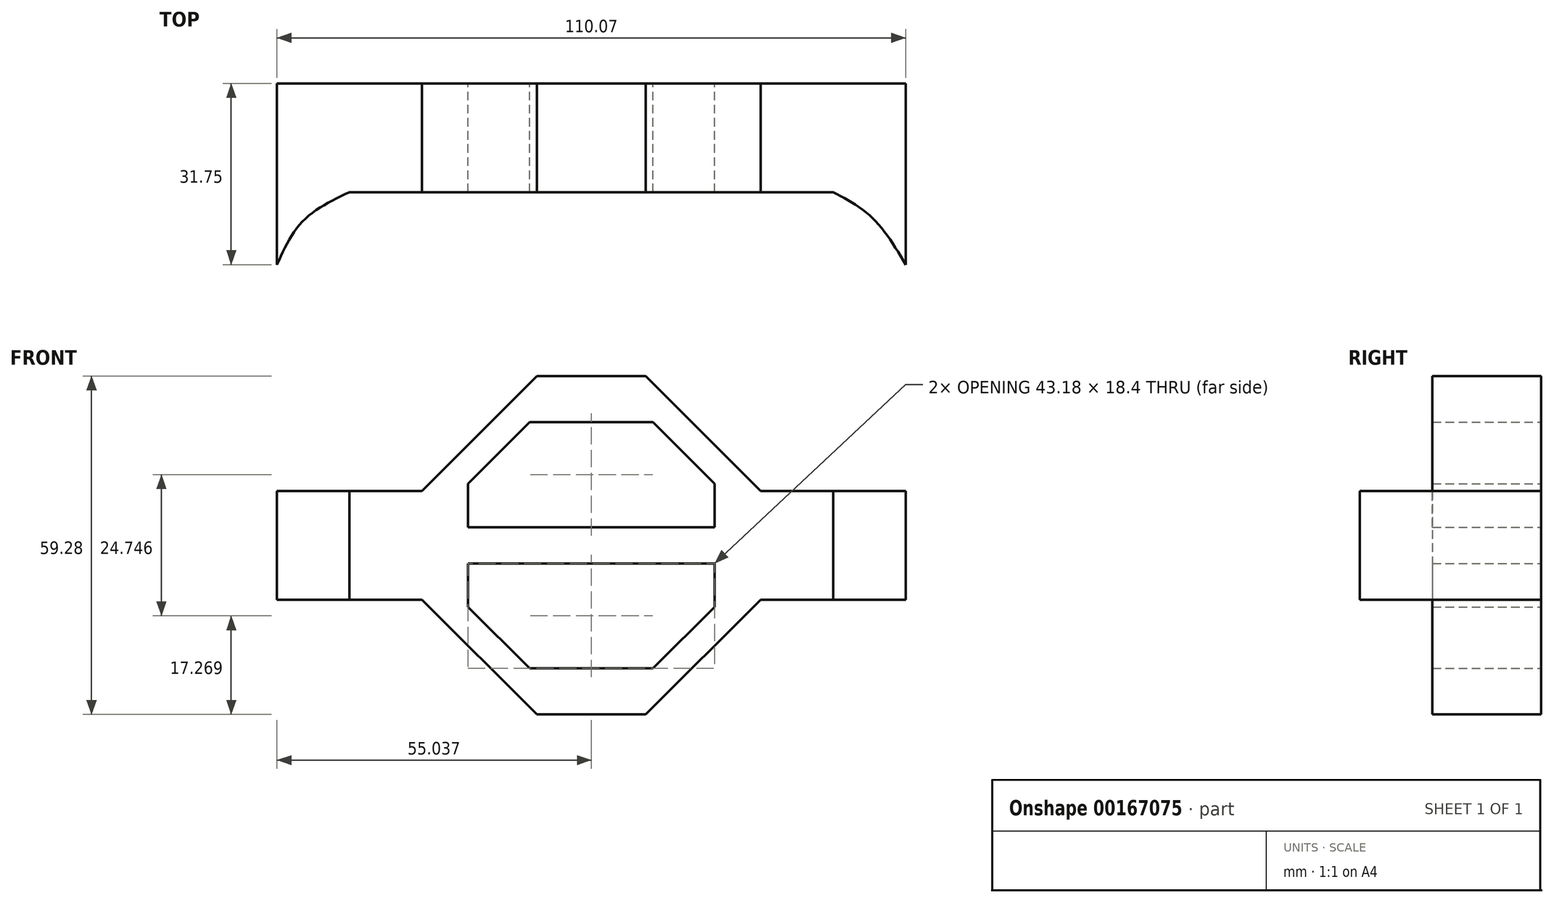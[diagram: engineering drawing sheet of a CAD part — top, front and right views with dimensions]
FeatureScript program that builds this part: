
annotation { "Feature Type Name" : "Feature", "Feature Type Description" : "" }
export const myFeature = defineFeature(function(context is Context, id is Id, definition is map)
    precondition{}
    {
        {
            var Q0;
            Q0=qCreatedBy(makeId("Front.planeOp"),FACE);
            var sketch = newSketch(context, id + "F0", { "sketchPlane" : qUnion([Q0])});
            skLineSegment(sketch, "E0", {"start": v(-40.98, 43.13) * mm, "end": v(-21.93, 43.13) * mm});
            skLineSegment(sketch, "E1", {"start": v(-21.93, 43.13) * mm, "end": v(-1.82, 23.02) * mm});
            skLineSegment(sketch, "E2", {"start": v(-1.82, 3.97) * mm, "end": v(-21.93, -16.15) * mm});
            skLineSegment(sketch, "E3", {"start": v(-21.93, -16.15) * mm, "end": v(-40.98, -16.15) * mm});
            skLineSegment(sketch, "E4", {"start": v(-40.98, -16.15) * mm, "end": v(-61.1, 3.97) * mm});
            skLineSegment(sketch, "E5", {"start": v(-61.1, 23.02) * mm, "end": v(-40.98, 43.13) * mm});
            skLineSegment(sketch, "E6", {"start": v(-1.82, 23.02) * mm, "end": v(10.88, 23.02) * mm});
            skLineSegment(sketch, "E7", {"start": v(10.88, 23.02) * mm, "end": v(10.88, 3.97) * mm});
            skLineSegment(sketch, "E8", {"start": v(10.88, 3.97) * mm, "end": v(-1.82, 3.97) * mm});
            skLineSegment(sketch, "E9", {"start": v(-61.1, 3.97) * mm, "end": v(-73.8, 3.97) * mm});
            skLineSegment(sketch, "E10", {"start": v(-73.8, 3.97) * mm, "end": v(-73.8, 23.02) * mm});
            skLineSegment(sketch, "E11", {"start": v(-73.8, 23.02) * mm, "end": v(-61.1, 23.02) * mm});
            skLineSegment(sketch, "E12", {"start": v(10.88, 23.02) * mm, "end": v(23.58, 23.02) * mm});
            skLineSegment(sketch, "E13", {"start": v(23.58, 23.02) * mm, "end": v(23.58, 3.97) * mm});
            skLineSegment(sketch, "E14", {"start": v(23.58, 3.97) * mm, "end": v(10.88, 3.97) * mm});
            skLineSegment(sketch, "E15", {"start": v(-73.8, 23.02) * mm, "end": v(-86.5, 23.02) * mm});
            skLineSegment(sketch, "E16", {"start": v(-86.5, 23.02) * mm, "end": v(-86.5, 3.97) * mm});
            skLineSegment(sketch, "E17", {"start": v(-86.5, 3.97) * mm, "end": v(-73.8, 3.97) * mm});
            skLineSegment(sketch, "E18", {"start": v(-9.86, 10.32) * mm, "end": v(-9.86, 2.7) * mm});
            skLineSegment(sketch, "E19", {"start": v(-9.86, 2.7) * mm, "end": v(-20.64, -8.08) * mm});
            skLineSegment(sketch, "E20", {"start": v(-53.04, 10.32) * mm, "end": v(-53.04, 2.7) * mm});
            skLineSegment(sketch, "E21", {"start": v(-53.04, 2.7) * mm, "end": v(-42.27, -8.08) * mm});
            skLineSegment(sketch, "E22", {"start": v(-42.27, -8.08) * mm, "end": v(-20.64, -8.08) * mm});
            skLineSegment(sketch, "E23", {"start": v(-53.04, 10.32) * mm, "end": v(-9.86, 10.32) * mm});
            skLineSegment(sketch, "E24", {"start": v(-53.04, 16.67) * mm, "end": v(-53.04, 24.29) * mm});
            skLineSegment(sketch, "E25", {"start": v(-53.04, 24.29) * mm, "end": v(-42.27, 35.06) * mm});
            skLineSegment(sketch, "E26", {"start": v(-9.86, 16.67) * mm, "end": v(-9.86, 24.29) * mm});
            skLineSegment(sketch, "E27", {"start": v(-9.86, 24.29) * mm, "end": v(-20.64, 35.06) * mm});
            skLineSegment(sketch, "E28", {"start": v(-20.64, 35.06) * mm, "end": v(-42.27, 35.06) * mm});
            skLineSegment(sketch, "E29", {"start": v(-9.86, 16.67) * mm, "end": v(-53.04, 16.67) * mm});
            skSolve(sketch);
        }
        {
            var Q0;
            Q0 = qSketchRegion(id + "F0", true);
            extrude(context, id + "F1", {"entities" : qUnion([Q0]), "depth" : 19.05 * mm});
        }
        {
            var Q0;
            Q0=makeQuery(id+"F1.opExtrude","SWEPT_FACE",FACE,{"disambiguationData":[OSD([sQuery(id+"F0.wireOp",EDGE,"E8"),sQuery(id+"F0.wireOp",EDGE,"E14")])]});
            var sketch = newSketch(context, id + "F2", { "sketchPlane" : qUnion([Q0])});
            skLineSegment(sketch, "E30", {"start": v(23.58, 19.05) * mm, "end": v(23.58, 31.75) * mm});
            skFitSpline(sketch, "E31", {"points": [v(10.88, 19.05) * mm, v(17.7, 23.5) * mm, v(23.58, 31.75) * mm], "startDerivative": vector(15.21, 7.92) * mm, "endDerivative": vector(10.28, 17.3) * mm});
            skSolve(sketch);
        }
        {
            var Q0;
            {var subQ0=sQuery(id+"F2.wireOp",EDGE,"E30");Q0=makeQuery(id+"F2.imprint","IMPRINT",FACE,{"disambiguationData":[TD([[makeQuery(id+"F2.imprint","IMPRINT",EDGE,{"derivedFrom":subQ0}),1.0]])]});}
            extrude(context, id + "F3", {"entities" : qUnion([Q0]), "operationType" : NewBodyOperationType.ADD, "oppositeDirection" : true, "depth" : 19.05 * mm});
        }
        {
            var Q0;
            Q0=makeQuery(id+"F1.opExtrude","SWEPT_FACE",FACE,{"disambiguationData":[OSD([sQuery(id+"F0.wireOp",EDGE,"E9"),sQuery(id+"F0.wireOp",EDGE,"E17")])]});
            var sketch = newSketch(context, id + "F4", { "sketchPlane" : qUnion([Q0])});
            skLineSegment(sketch, "E32", {"start": v(-86.5, 19.05) * mm, "end": v(-86.5, 31.75) * mm});
            skFitSpline(sketch, "E33", {"points": [v(-73.8, 19.05) * mm, v(-81.9, 24.04) * mm, v(-86.5, 31.75) * mm], "startDerivative": vector(-17.67, 8.36) * mm, "endDerivative": vector(-7.68, 17.08) * mm});
            skSolve(sketch);
        }
        {
            var Q0;
            {var subQ0=sQuery(id+"F4.wireOp",EDGE,"E32");Q0=makeQuery(id+"F4.imprint","IMPRINT",FACE,{"disambiguationData":[TD([[makeQuery(id+"F4.imprint","IMPRINT",EDGE,{"derivedFrom":subQ0}),-1.0]])]});}
            extrude(context, id + "F5", {"entities" : qUnion([Q0]), "operationType" : NewBodyOperationType.ADD, "oppositeDirection" : true, "depth" : 19.05 * mm});
        }
    });
